# Revit family: Урна уличная «Радиус» Арт 7281
name_source: partatom
category: Антураж
revit_build: Autodesk Revit 2018 (Build: 20180423_1000(x64)
units: mm (PartAtom-declared; Revit-internal decimal feet)

## family parameters
Всегда вертикально = Да
Источник визуального образа = Геометрия семейства
На основе рабочей плоскости = Нет
Общий = Нет
При загрузке вырезать с полостями = Нет
Точка расчета площади = Нет

## types (2) — shared parameters
URL = https://hobbyka.ru
Артикул товара = Арт. 7281
Высота = 580 мм
Группа модели = Уличные урны
Диаметр = 400 мм
Длина = 400 мм
Изготовитель = ООО «Хоббика»
Изображение типоразмера = Урна уличная «Радиус» Арт 7281.jpg
Материал изделия = Сталь, дерево
Цвет отделки = Дерево
Ширина = 400 мм

## per-type parameters (varying)
| type | Нержавеющая сталь | Объём 30 литров | Описание | Цвет урны |
| Урна уличная «Радиус». Версия Нержавеющая сталь | Да | Нет | Урна уличная «Радиус». Версия: Нержавеющая сталь | Нержавеющая сталь |
| Урна уличная «Радиус». Версия Объём 30 литров | Нет | Да | Урна уличная «Радиус». Версия: Объём 30 литров | Сталь |
